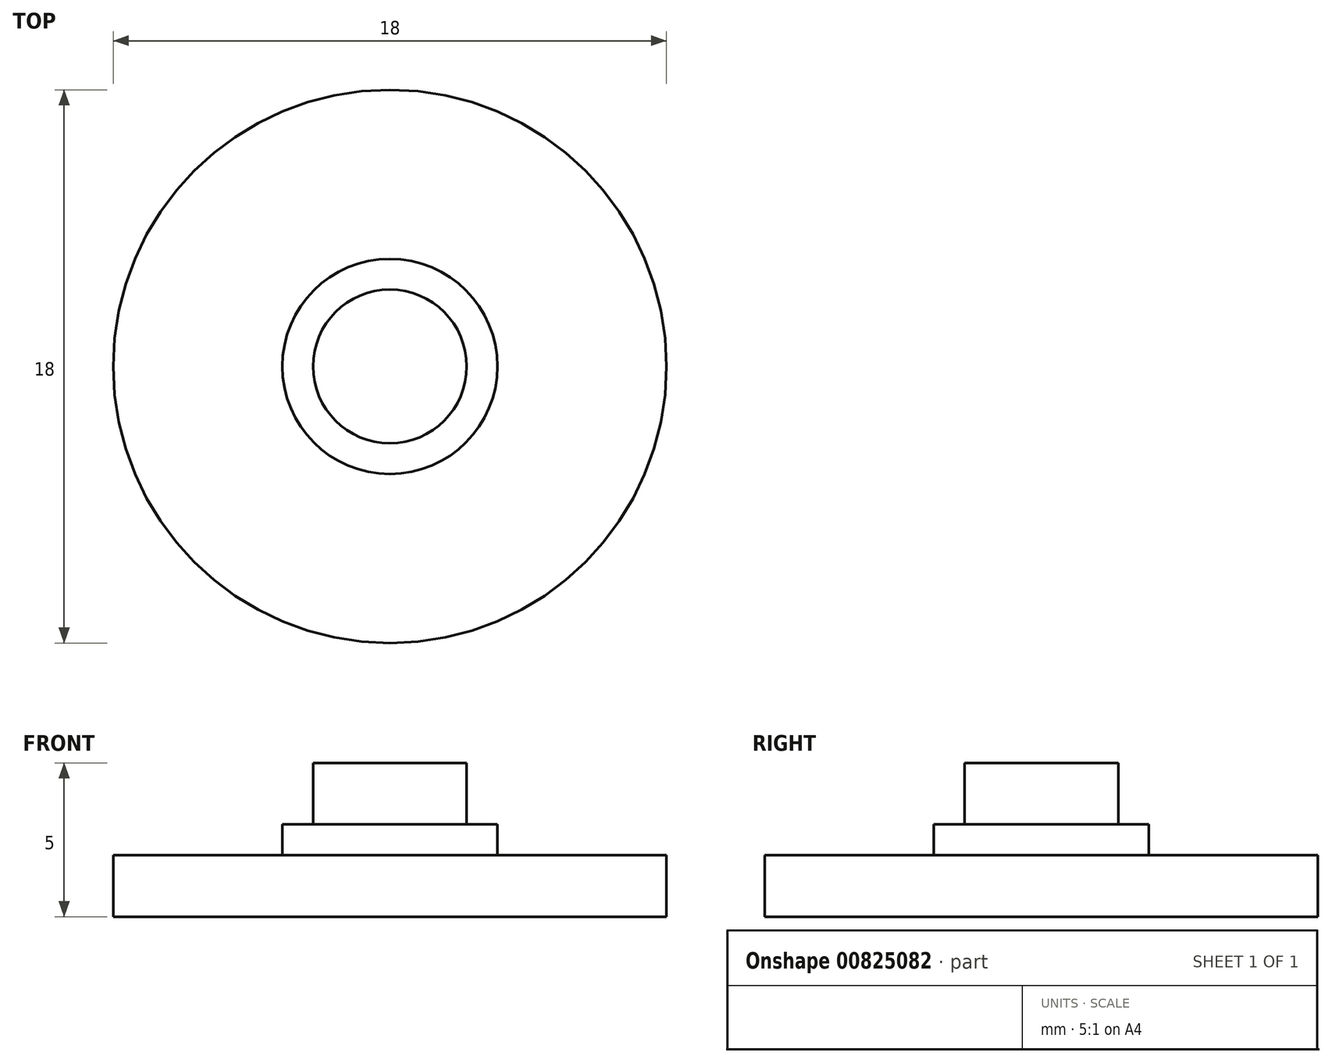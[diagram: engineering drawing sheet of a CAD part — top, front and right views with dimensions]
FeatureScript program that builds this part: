
annotation { "Feature Type Name" : "Feature", "Feature Type Description" : "" }
export const myFeature = defineFeature(function(context is Context, id is Id, definition is map)
    precondition{}
    {
        {
            var Q0;
            Q0=qCreatedBy(makeId("Top.planeOp"),FACE);
            var sketch = newSketch(context, id + "F0", { "sketchPlane" : qUnion([Q0])});
            skCircle(sketch, "E0", {"center": v(0, 0) * mm, "radius": 9 * mm});
            skCircle(sketch, "E1", {"center": v(0, 0) * mm, "radius": 3.5 * mm});
            skCircle(sketch, "E2", {"center": v(0, 0) * mm, "radius": 2.5 * mm});
            skSolve(sketch);
        }
        {
            var Q0;
            Q0=makeQuery(id+"F0.imprint","IMPRINT",FACE,{"disambiguationData":[TD([[makeQuery(id+"F0.imprint","IMPRINT",EDGE,{"derivedFrom":sQuery(id+"F0.wireOp",EDGE,"E0")}),1.0]])]});
            var sketch = newSketch(context, id + "F1", { "sketchPlane" : qUnion([Q0])});
            skSolve(sketch);
        }
        {
            var Q0;
            Q0 = qSketchRegion(id + "F1", true);
            var Q1;
            Q1=makeQuery(id+"F1.imprint","IMPRINT",FACE,{"disambiguationData":[TD([[makeQuery(id+"F1.imprint","IMPRINT",EDGE,{"derivedFrom":makeQuery(id+"F0.imprint","IMPRINT",EDGE,{"derivedFrom":sQuery(id+"F0.wireOp",EDGE,"E0")})}),1.0]])]});
            extrude(context, id + "F2", {"entities" : qUnion([Q0, Q1]), "depth" : 2 * mm, "offsetDistance" : 25 * mm});
        }
        {
            var Q0;
            Q0=makeQuery(id+"F0.imprint","IMPRINT",FACE,{"disambiguationData":[TD([[makeQuery(id+"F0.imprint","IMPRINT",EDGE,{"derivedFrom":sQuery(id+"F0.wireOp",EDGE,"E1")}),1.0]])]});
            var sketch = newSketch(context, id + "F3", { "sketchPlane" : qUnion([Q0])});
            skSolve(sketch);
        }
        {
            var Q0;
            Q0 = qSketchRegion(id + "F3", true);
            var Q1;
            Q1=makeQuery(id+"F0.imprint","IMPRINT",FACE,{"disambiguationData":[TD([[makeQuery(id+"F0.imprint","IMPRINT",EDGE,{"derivedFrom":sQuery(id+"F0.wireOp",EDGE,"E1")}),1.0]])]});
            extrude(context, id + "F4", {"entities" : qUnion([Q0, Q1]), "operationType" : NewBodyOperationType.ADD, "depth" : 3 * mm, "offsetDistance" : 25 * mm});
        }
        {
            var Q0;
            Q0=qCreatedBy(makeId("Top.planeOp"),FACE);
            var sketch = newSketch(context, id + "F5", { "sketchPlane" : qUnion([Q0])});
            skCircle(sketch, "E3", {"center": v(0, 0) * mm, "radius": 2.5 * mm});
            skSolve(sketch);
        }
        {
            var Q0;
            Q0 = qSketchRegion(id + "F5", true);
            var Q1;
            Q1=makeQuery(id+"F3.imprint","IMPRINT",FACE,{"disambiguationData":[TD([[makeQuery(id+"F3.imprint","IMPRINT",EDGE,{"derivedFrom":makeQuery(id+"F0.imprint","IMPRINT",EDGE,{"derivedFrom":sQuery(id+"F0.wireOp",EDGE,"E2")})}),1.0]])]});
            extrude(context, id + "F6", {"entities" : qUnion([Q0, Q1]), "operationType" : NewBodyOperationType.ADD, "depth" : 5 * mm, "offsetDistance" : 25 * mm});
        }
    });
